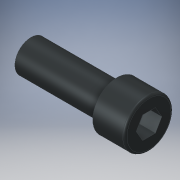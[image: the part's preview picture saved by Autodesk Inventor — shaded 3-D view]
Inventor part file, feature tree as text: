
AUTODESK INVENTOR PART (.ipt)
format: ipt  version: 2019 (Build 230136000, 136)  size: 126,976 bytes
history: native  units: mm
features: extrude x3, sketch x3, plane x1, fillet x1
ambient origin geometry x8: Origin, YZ Plane, XZ Plane, XY Plane, X Axis, Y Axis, Z Axis, Center Point
bodies: Solid1 (feature_tree)
feature tree (8):
  extrude  "Extrusion1"  Depth=8.0mm TaperAngle=0.0deg
  extrude  "Extrusion2"  Depth=3.0mm TaperAngle=0.0deg
  plane  "Work Plane1"
  fillet  "Fillet2"  Radius=0.2mm
  extrude  "Extrusion4"  Depth=1.5mm
  sketch  "Sketch1"  dims[d0=3.0mm d1=8.0mm d2=0.0mm]
  sketch  "Sketch2"  dims[d3=4.5mm d4=3.0mm d5=0.0mm d13=0.2mm]
  sketch  "Sketch4"  dims[d14=2.4mm d15=1.03923mm d16=1.5mm d17=0.0mm]
